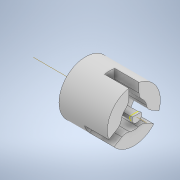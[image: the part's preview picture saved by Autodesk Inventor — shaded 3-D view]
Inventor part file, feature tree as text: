
AUTODESK INVENTOR PART (.ipt)
format: ipt  version: 2022.6 (Build 266554000, 554)  size: 214,528 bytes
history: native  units: mm
features: sketch x8, extrude x5, projected_geometry x4, fillet x1, plane x1, loft x1, other x1
ambient origin geometry x8: Origin, YZ Plane, XZ Plane, XY Plane, X Axis, Y Axis, Z Axis, Center Point
bodies: Solid1 (feature_tree)
feature tree (21):
  extrude  "Extrusion1"  Depth=0.5mm
  extrude  "Extrusion2"  Depth=17.5mm
  extrude  "Extrusion3"  Depth=8.5mm
  extrude  "Extrusion4"  Depth=4.0mm
  fillet  "Fillet1"  Radius=30.0mm
  extrude  "Extrusion5"  Depth=13.3mm
  sketch  "Sketch6"  dims[d20=7.0mm d21=0.0mm d22=10.0mm]
  plane  "Work Plane1"
  sketch  "Sketch7"  dims[d23=3.0mm]
  sketch  "Sketch8"  dims[d24=5.0mm d25=20.0mm d26=0.0mm d27=1.0mm d28=3.2mm d30=0.5mm d31=0.7mm d32=0.0mm d33=90.0deg d34=0.0mm d35=90.0deg d29=0.5mm]
  loft  "Loft1"
  sketch  "Sketch1"  dims[d1=2.8mm d2=0.5mm]
  sketch  "Sketch2"  dims[d3=8.0mm d4=0.0mm d5=17.5mm]
  sketch  "Sketch3"  dims[d6=8.0mm d7=0.0mm d8=8.5mm]
  projected_geometry  "Projected Loop1"
  sketch  "Sketch4"  dims[d9=3.4mm d10=4.0mm d12=30.0mm d14=360.0deg]
  sketch  "Sketch5"  dims[d16=8.0mm d17=0.0mm d19=13.3mm]
  projected_geometry  "Projected Loop2"
  projected_geometry  "Projected Loop3"
  projected_geometry  "Projected Loop4"
  other  "Edges1"
